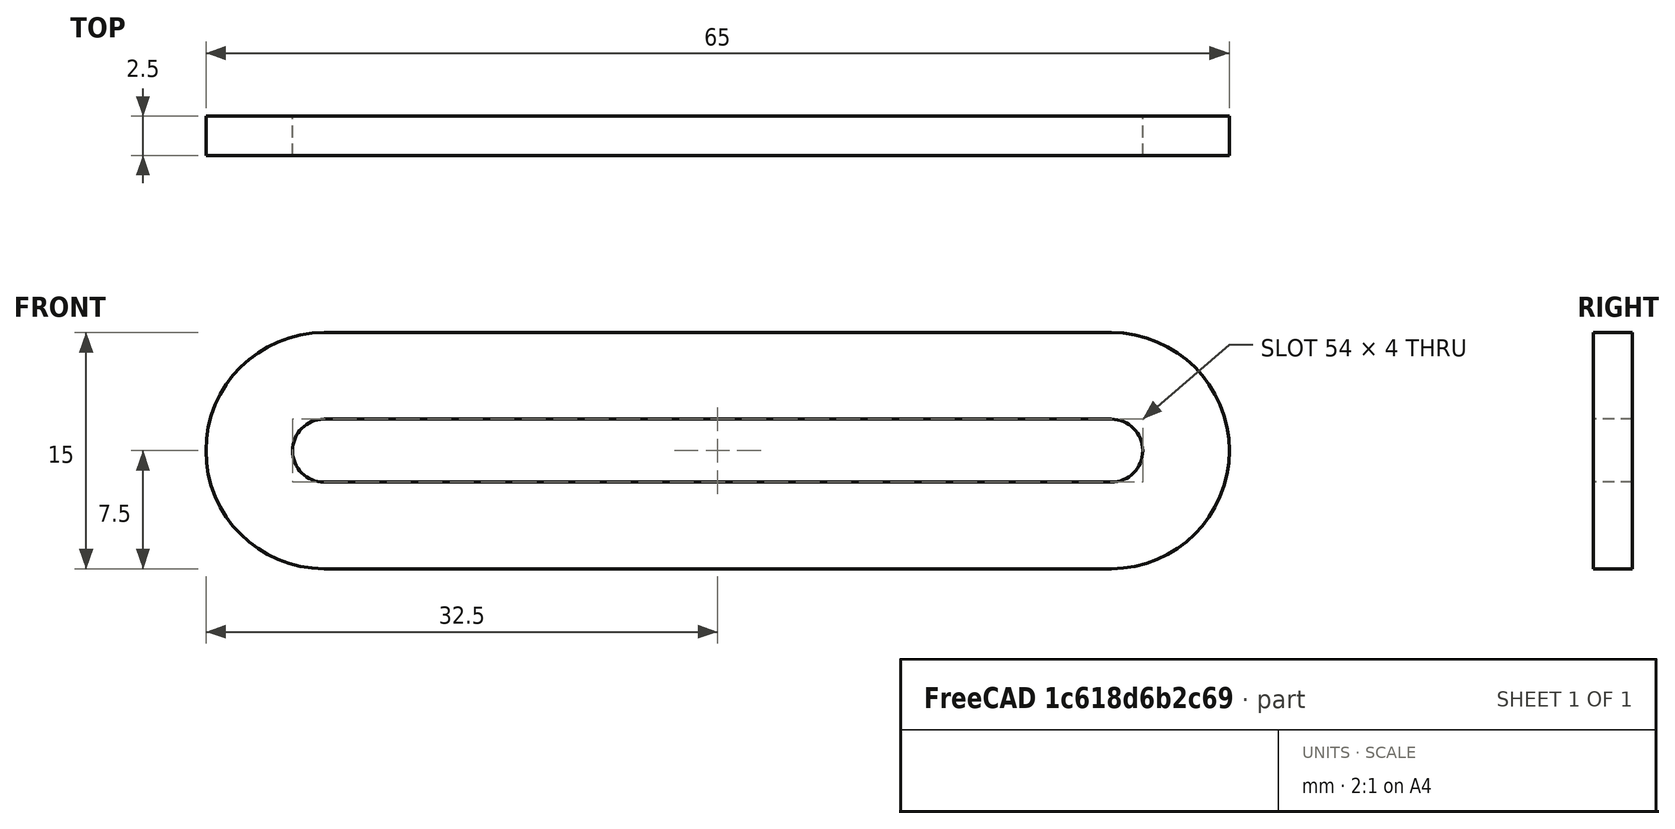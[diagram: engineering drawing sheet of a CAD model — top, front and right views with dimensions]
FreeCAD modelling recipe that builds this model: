
FCSTD DOCUMENT  (FreeCAD 0.21R33668 +26 (Git))
Label: cover_side
License: All rights reserved
LicenseURL: https://en.wikipedia.org/wiki/All_rights_reserved
objects: Sketcher::SketchObject×1, PartDesign::Pad×1, PartDesign::Body×1
note: 4 computed .brp shape members not serialized (recipe doc carries the construction recipe); baked Part::Feature solids carry a one-line shape summary decoded from their .brp

FEATURE [Sketcher::SketchObject] Sketch
  FullyConstrained = true
  MapMode = 5
  Placement = pos=(0,0,0) rot=(1,0,0;1.5708rad)
  Support = -> [XZ_Plane]
  sketch-geometry (8):
    g0: ArcOfCircle CenterX=0 CenterY=0 CenterZ=0 NormalX=0 NormalY=0 NormalZ=1 AngleXU=0 Radius=7.5 StartAngle=1.5708 EndAngle=4.71239
    g1: ArcOfCircle CenterX=50 CenterY=0 CenterZ=0 NormalX=0 NormalY=0 NormalZ=1 AngleXU=0 Radius=7.5 StartAngle=4.71239 EndAngle=7.85398
    g2: LineSegment StartX=-1.4e-15 StartY=-7.5 StartZ=0 EndX=50 EndY=-7.5 EndZ=0
    g3: LineSegment StartX=50 StartY=7.5 StartZ=0 EndX=0 EndY=7.5 EndZ=0
    g4: ArcOfCircle CenterX=0 CenterY=0 CenterZ=0 NormalX=0 NormalY=0 NormalZ=1 AngleXU=0 Radius=2 StartAngle=1.5708 EndAngle=4.71239
    g5: ArcOfCircle CenterX=50 CenterY=0 CenterZ=0 NormalX=0 NormalY=0 NormalZ=1 AngleXU=0 Radius=2 StartAngle=4.71239 EndAngle=7.85398
    g6: LineSegment StartX=-4e-16 StartY=-2 StartZ=0 EndX=50 EndY=-2 EndZ=0
    g7: LineSegment StartX=50 StartY=2 StartZ=0 EndX=0 EndY=2 EndZ=0
  constraints (18):
    c: Tangent(g0,g2) = -1.5708
    c: Tangent(g2,g1) = -1.5708
    c: Tangent(g1,g3) = -1.5708
    c: Tangent(g3,g0) = -1.5708
    c: Equal(g0,g1)
    c: Coincident(g0,g-1)
    c: DistanceY(g1,g1) = 15
    c: Horizontal(g0,g1)
    c: DistanceX(g3,g3) = 50
    c: Tangent(g4,g6) = -1.5708
    c: Tangent(g6,g5) = -1.5708
    c: Tangent(g5,g7) = -1.5708
    c: Tangent(g7,g4) = -1.5708
    c: Equal(g4,g5)
    c: Coincident(g4,g0)
    c: DistanceY(g5,g5) = 4
    c: Horizontal(g5,g1)
    c: Vertical(g5,g1)
FEATURE [PartDesign::Pad] Pad
  Direction = (0,-1,2e-16)
  Length = 2.5
  Length2 = 10
  Placement = pos=(0,0,0) rot=(1,0,0;1.5708rad)
  Profile = -> Sketch
  ReferenceAxis = -> Sketch [N_Axis]
  Type = 0
FEATURE [PartDesign::Body] Body
  Group = -> [Sketch,Pad]
  Origin = -> Origin
  Tip = -> Pad
